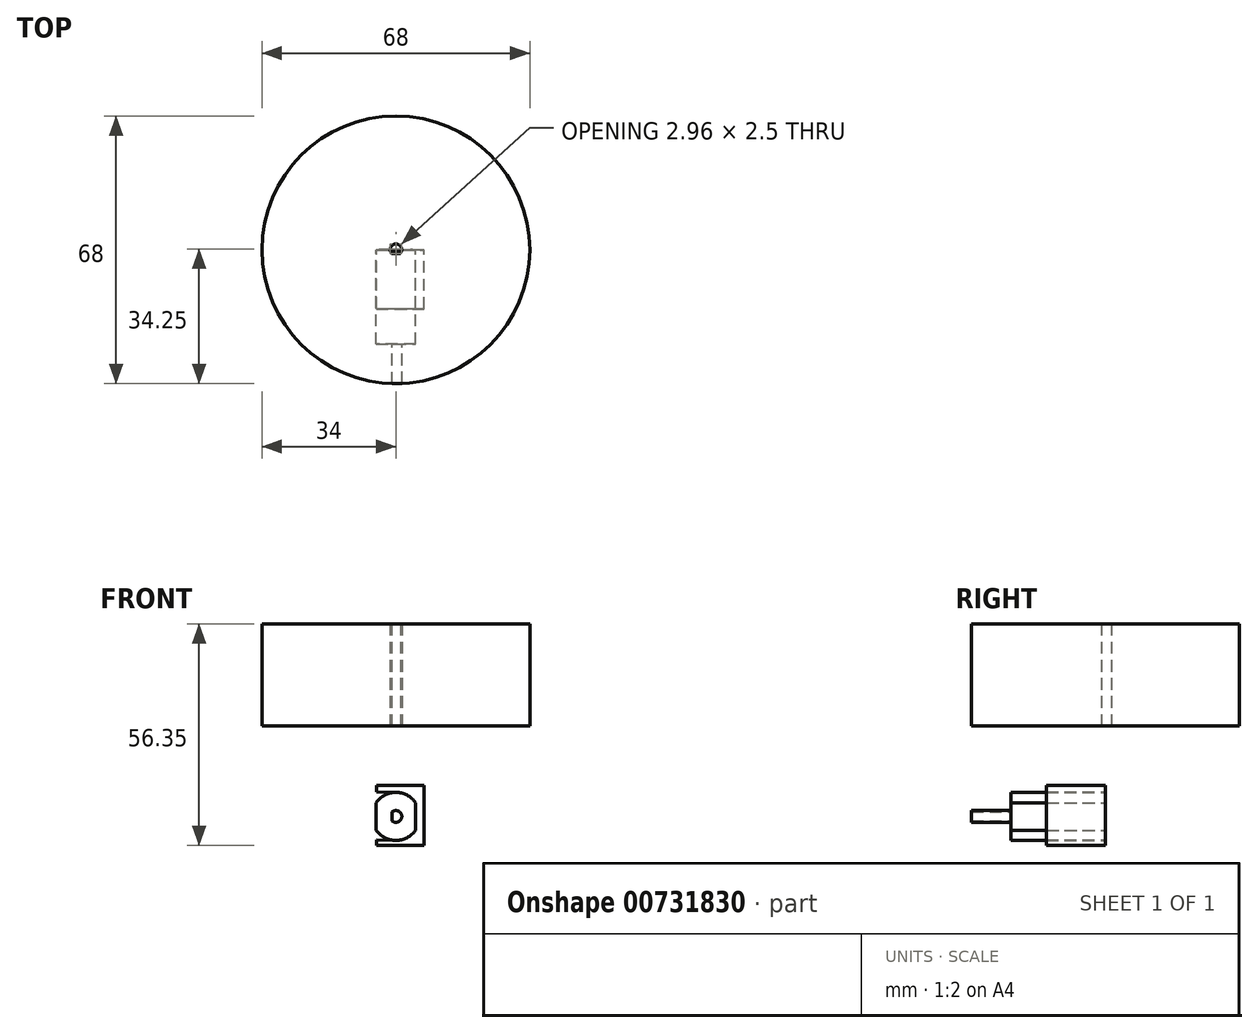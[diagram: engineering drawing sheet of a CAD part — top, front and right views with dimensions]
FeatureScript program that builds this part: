
annotation { "Feature Type Name" : "Feature", "Feature Type Description" : "" }
export const myFeature = defineFeature(function(context is Context, id is Id, definition is map)
    precondition{}
    {
        {
            var Q0;
            Q0=qCreatedBy(makeId("Top.planeOp"),FACE);
            var sketch = newSketch(context, id + "F0", { "sketchPlane" : qUnion([Q0])});
            skCircle(sketch, "E0", {"center": v(0, 0) * mm, "radius": 34 * mm});
            skArc(sketch, "E1", {"start": v(1.12, -1) * mm, "mid": v(0, 1.5) * mm, "end": v(-1.12, -1) * mm});
            skLineSegment(sketch, "E2", {"start": v(0, 0) * mm, "end": v(0, -1) * mm});
            skLineSegment(sketch, "E3", {"start": v(0, -1) * mm, "end": v(1.12, -1) * mm});
            skLineSegment(sketch, "E4", {"start": v(1.12, -1) * mm, "end": v(-1.12, -1) * mm});
            skSolve(sketch);
        }
        {
            var Q0;
            Q0=makeQuery(id+"F0.imprint","IMPRINT",FACE,{"disambiguationData":[TD([[makeQuery(id+"F0.imprint","IMPRINT",EDGE,{"derivedFrom":sQuery(id+"F0.wireOp",EDGE,"E0")}),1.0]])]});
            extrude(context, id + "F1", {"entities" : qUnion([Q0]), "depth" : 26 * mm, "offsetDistance" : 25 * mm});
        }
        {
            var Q0;
            Q0=qCreatedBy(makeId("Front.planeOp"),FACE);
            var sketch = newSketch(context, id + "F2", { "sketchPlane" : qUnion([Q0])});
            skArc(sketch, "E5", {"start": v(5, -19.46) * mm, "mid": v(0, -16.86) * mm, "end": v(-5, -19.46) * mm});
            skLineSegment(sketch, "E6.left", {"start": v(5, -19.46) * mm, "end": v(5, -26.46) * mm});
            skLineSegment(sketch, "E6.right", {"start": v(-5, -19.46) * mm, "end": v(-5, -26.46) * mm});
            skArc(sketch, "E7.trimOffspring", {"start": v(-5, -26.46) * mm, "mid": v(0, -29.06) * mm, "end": v(5, -26.46) * mm});
            skArc(sketch, "E8", {"start": v(-1, -24.08) * mm, "mid": v(1.5, -22.96) * mm, "end": v(-1, -21.84) * mm});
            skLineSegment(sketch, "E9", {"start": v(-1, -22.96) * mm, "end": v(-1, -21.84) * mm});
            skLineSegment(sketch, "E10", {"start": v(-1, -21.84) * mm, "end": v(-1, -24.08) * mm});
            skLineSegment(sketch, "E11", {"start": v(5, -19.46) * mm, "end": v(5, -17) * mm});
            skLineSegment(sketch, "E12", {"start": v(5, -17) * mm, "end": v(-4.94, -16.7) * mm});
            skLineSegment(sketch, "E13", {"start": v(-4.94, -16.7) * mm, "end": v(-4.94, -15.02) * mm});
            skLineSegment(sketch, "E14", {"start": v(-4.94, -15.02) * mm, "end": v(7.14, -15.02) * mm});
            skLineSegment(sketch, "E15", {"start": v(7.14, -15.02) * mm, "end": v(7.14, -30.35) * mm});
            skLineSegment(sketch, "E16", {"start": v(7.14, -30.35) * mm, "end": v(-4.94, -30.35) * mm});
            skLineSegment(sketch, "E17", {"start": v(-4.94, -30.35) * mm, "end": v(-4.94, -28.96) * mm});
            skLineSegment(sketch, "E18", {"start": v(-4.94, -28.96) * mm, "end": v(5, -29.17) * mm});
            skLineSegment(sketch, "E19", {"start": v(5, -29.17) * mm, "end": v(5, -26.46) * mm});
            skSolve(sketch);
        }
        {
            var Q0;
            {var subQ0=sQuery(id+"F2.wireOp",EDGE,"E8");Q0=makeQuery(id+"F2.imprint","IMPRINT",FACE,{"disambiguationData":[TD([[makeQuery(id+"F2.imprint","IMPRINT",EDGE,{"derivedFrom":subQ0}),1.0]])]});}
            extrude(context, id + "F3", {"entities" : qUnion([Q0]), "depth" : 34 * mm, "offsetDistance" : 25 * mm});
        }
        {
            var Q0;
            Q0=makeQuery(id+"F2.imprint","IMPRINT",FACE,{"disambiguationData":[TD([[makeQuery(id+"F2.imprint","IMPRINT",EDGE,{"derivedFrom":sQuery(id+"F2.wireOp",EDGE,"E5")}),1.0]])]});
            extrude(context, id + "F4", {"entities" : qUnion([Q0]), "operationType" : NewBodyOperationType.ADD, "depth" : 24 * mm, "offsetDistance" : 25 * mm});
        }
        {
            var Q0;
            Q0=makeQuery(id+"F2.imprint","IMPRINT",FACE,{"disambiguationData":[TD([[makeQuery(id+"F2.imprint","IMPRINT",EDGE,{"derivedFrom":sQuery(id+"F2.wireOp",EDGE,"E6.left")}),1.0]])]});
            var Q1;
            {var subQ0=sQuery(id+"F2.wireOp",EDGE,"E19");Q1=makeQuery(id+"F2.imprint","IMPRINT",FACE,{"disambiguationData":[TD([[makeQuery(id+"F2.imprint","IMPRINT",EDGE,{"derivedFrom":subQ0}),1.0]])]});}
            var Q2;
            {var subQ0=sQuery(id+"F2.wireOp",EDGE,"E11");Q2=makeQuery(id+"F2.imprint","IMPRINT",FACE,{"disambiguationData":[TD([[makeQuery(id+"F2.imprint","IMPRINT",EDGE,{"derivedFrom":subQ0}),1.0]])]});}
            extrude(context, id + "F5", {"entities" : qUnion([Q0, Q1, Q2]), "depth" : 15 * mm, "offsetDistance" : 25 * mm});
        }
    });
